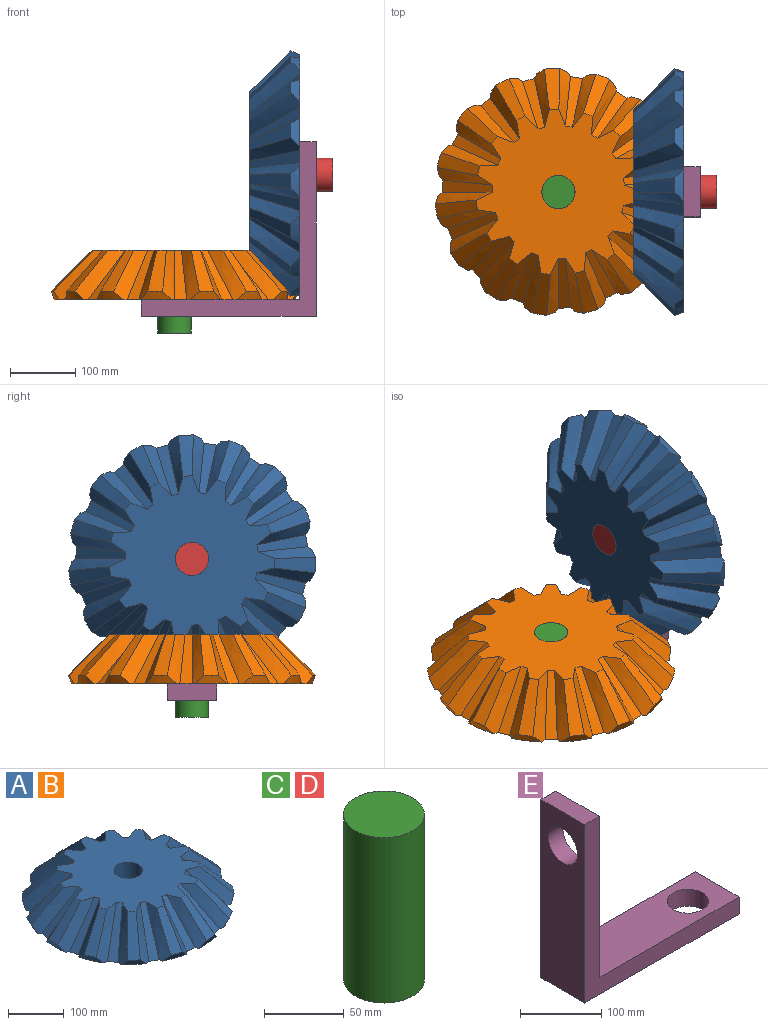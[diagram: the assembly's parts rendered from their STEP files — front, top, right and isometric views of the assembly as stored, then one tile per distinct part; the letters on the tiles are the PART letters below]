
ASSEMBLY  parts=5 mates=6
PART A: 78 faces, bbox 408.6x408.6x76.2 mm
  f0: plane 368.3x367.72mm, normal (0,0,-1), area 102263.9mm2, adj f2,f4,f6,f8,f10,f12,f14,f16
  f1: cone r=203.2mm half-angle=45deg, axis (0,0,-1), area 1668.1mm2, adj f2,f30,f33,f74
  f2: cone r=189.73mm half-angle=22.5deg, axis (0,0,1), area 520mm2, adj f0,f1,f33,f74
  f3: cone r=203.2mm half-angle=45deg, axis (0,0,-1), area 1668.1mm2, adj f4,f30,f71,f75
  f4: cone r=189.73mm half-angle=22.5deg, axis (0,0,1), area 520mm2, adj f0,f3,f71,f75
  f5: cone r=203.2mm half-angle=45deg, axis (0,0,-1), area 1668.1mm2, adj f6,f30,f68,f72
  f6: cone r=189.73mm half-angle=22.5deg, axis (0,0,1), area 520mm2, adj f0,f5,f68,f72
  f7: cone r=203.2mm half-angle=45deg, axis (0,0,-1), area 1668.1mm2, adj f8,f30,f65,f69
  f8: cone r=189.73mm half-angle=22.5deg, axis (0,0,1), area 520mm2, adj f0,f7,f65,f69
  f9: cone r=203.2mm half-angle=45deg, axis (0,0,-1), area 1668.1mm2, adj f10,f30,f62,f66
  f10: cone r=189.73mm half-angle=22.5deg, axis (0,0,1), area 520mm2, adj f0,f9,f62,f66
  f11: cone r=203.2mm half-angle=45deg, axis (0,0,-1), area 1668.1mm2, adj f12,f30,f59,f63
  f12: cone r=189.73mm half-angle=22.5deg, axis (0,0,1), area 520mm2, adj f0,f11,f59,f63
  f13: cone r=203.2mm half-angle=45deg, axis (0,0,-1), area 1668.1mm2, adj f14,f30,f56,f60
  f14: cone r=189.73mm half-angle=22.5deg, axis (0,0,1), area 520mm2, adj f0,f13,f56,f60
  f15: cone r=203.2mm half-angle=45deg, axis (0,0,-1), area 1668.1mm2, adj f16,f30,f53,f57
  f16: cone r=189.73mm half-angle=22.5deg, axis (0,0,1), area 520mm2, adj f0,f15,f53,f57
  f17: cone r=203.2mm half-angle=45deg, axis (0,0,-1), area 1668.1mm2, adj f18,f30,f50,f54
  f18: cone r=189.73mm half-angle=22.5deg, axis (0,0,1), area 520mm2, adj f0,f17,f50,f54
  f19: cone r=203.2mm half-angle=45deg, axis (0,0,-1), area 1668.1mm2, adj f20,f30,f47,f51
  f20: cone r=189.73mm half-angle=22.5deg, axis (0,0,1), area 520mm2, adj f0,f19,f47,f51
  f21: cone r=203.2mm half-angle=45deg, axis (0,0,-1), area 1668.1mm2, adj f22,f30,f44,f48
  f22: cone r=189.73mm half-angle=22.5deg, axis (0,0,1), area 520mm2, adj f0,f21,f44,f48
  f23: cone r=203.2mm half-angle=45deg, axis (0,0,-1), area 1668.1mm2, adj f24,f30,f41,f45
  f24: cone r=189.73mm half-angle=22.5deg, axis (0,0,1), area 520mm2, adj f0,f23,f41,f45
  f25: cone r=203.2mm half-angle=45deg, axis (0,0,-1), area 1668.1mm2, adj f26,f30,f38,f42
  f26: cone r=189.73mm half-angle=22.5deg, axis (0,0,1), area 520mm2, adj f0,f25,f38,f42
  f27: cone r=203.2mm half-angle=45deg, axis (0,0,-1), area 1668.1mm2, adj f28,f30,f35,f39
  f28: cone r=189.73mm half-angle=22.5deg, axis (0,0,1), area 520mm2, adj f0,f27,f35,f39
  f29: cone r=203.2mm half-angle=45deg, axis (0,0,-1), area 1668.1mm2, adj f30,f31,f32,f36
  f30: plane 253.72x252.54mm, normal (0,0,1), area 39255.5mm2, adj f1,f3,f5,f7,f9,f11,f13,f15
  f31: cone r=189.73mm half-angle=22.5deg, axis (0,0,1), area 520mm2, adj f0,f29,f32,f36
  f32: bspline ~101.6x76.2mm, area 2318.6mm2, adj f0,f29,f30,f31,f34
  f33: bspline ~99.08x76.2mm, area 2314.1mm2, adj f0,f1,f2,f30,f34
  f34: plane 76.2x76.2mm, normal (0.71,0,0.71), area 1594.3mm2, adj f0,f30,f32,f33
  f35: bspline ~81.96x76.2mm, area 2318.6mm2, adj f0,f27,f28,f30,f37
  f36: bspline ~103.67x76.2mm, area 2314.1mm2, adj f0,f29,f30,f31,f37
  f37: plane 76.2x75.63mm, normal (0.65,-0.29,0.71), area 1594.3mm2, adj f0,f30,f35,f36
  f38: bspline ~93.36x76.2mm, area 2318.6mm2, adj f0,f25,f26,f30,f40
  f39: bspline ~87.82x76.2mm, area 2314.1mm2, adj f0,f27,f28,f30,f40
  f40: plane 76.2x66.53mm, normal (0.47,-0.53,0.71), area 1594.3mm2, adj f0,f30,f38,f39
  f41: bspline ~104.88x76.2mm, area 2318.6mm2, adj f0,f23,f24,f30,f43
  f42: bspline ~86.68x76.2mm, area 2314.1mm2, adj f0,f25,f26,f30,f43
  f43: plane 77.04x76.2mm, normal (0.22,-0.67,0.71), area 1594.3mm2, adj f0,f30,f41,f42
  f44: bspline ~98.25x76.2mm, area 2318.6mm2, adj f0,f21,f22,f30,f46
  f45: bspline ~103.83x76.2mm, area 2314.1mm2, adj f0,f23,f24,f30,f46
  f46: plane 77.33x76.2mm, normal (-0.07,-0.7,0.71), area 1594.3mm2, adj f0,f30,f44,f45
  f47: bspline ~76.2x74.64mm, area 2318.6mm2, adj f0,f19,f20,f30,f49
  f48: bspline ~101.33x76.2mm, area 2314.1mm2, adj f0,f21,f22,f30,f49
  f49: plane 76.2x73.39mm, normal (-0.35,-0.61,0.71), area 1594.3mm2, adj f0,f30,f47,f48
  f50: bspline ~97.89x76.2mm, area 2318.6mm2, adj f0,f17,f18,f30,f52
  f51: bspline ~81.31x76.2mm, area 2314.1mm2, adj f0,f19,f20,f30,f52
  f52: plane 76.2x70.34mm, normal (-0.57,-0.42,0.71), area 1594.3mm2, adj f0,f30,f50,f51
  f53: bspline ~104.93x76.2mm, area 2318.6mm2, adj f0,f15,f16,f30,f55
  f54: bspline ~93.83x76.2mm, area 2314.1mm2, adj f0,f17,f18,f30,f55
  f55: plane 77.61x76.2mm, normal (-0.69,-0.15,0.71), area 1594.3mm2, adj f0,f30,f53,f54
  f56: bspline ~93.83x76.2mm, area 2318.6mm2, adj f0,f13,f14,f30,f58
  f57: bspline ~104.93x76.2mm, area 2314.1mm2, adj f0,f15,f16,f30,f58
  f58: plane 77.61x76.2mm, normal (-0.69,0.15,0.71), area 1594.3mm2, adj f0,f30,f56,f57
  f59: bspline ~81.31x76.2mm, area 2318.6mm2, adj f0,f11,f12,f30,f61
  f60: bspline ~97.89x76.2mm, area 2314.1mm2, adj f0,f13,f14,f30,f61
  f61: plane 76.2x70.34mm, normal (-0.57,0.42,0.71), area 1594.3mm2, adj f0,f30,f59,f60
  f62: bspline ~98.03x76.2mm, area 2318.6mm2, adj f0,f9,f10,f30,f64
  f63: bspline ~76.2x74.64mm, area 2314.1mm2, adj f0,f11,f12,f30,f64
  f64: plane 76.2x73.39mm, normal (-0.35,0.61,0.71), area 1594.3mm2, adj f0,f30,f62,f63
  f65: bspline ~101.1x76.2mm, area 2318.6mm2, adj f0,f7,f8,f30,f67
  f66: bspline ~98.25x76.2mm, area 2314.1mm2, adj f0,f9,f10,f30,f67
  f67: plane 77.33x76.2mm, normal (-0.07,0.7,0.71), area 1594.3mm2, adj f0,f30,f65,f66
  f68: bspline ~86.68x76.2mm, area 2318.6mm2, adj f0,f5,f6,f30,f70
  f69: bspline ~104.88x76.2mm, area 2314.1mm2, adj f0,f7,f8,f30,f70
  f70: plane 77.04x76.2mm, normal (0.22,0.67,0.71), area 1594.3mm2, adj f0,f30,f68,f69
  f71: bspline ~87.82x76.2mm, area 2318.6mm2, adj f0,f3,f4,f30,f73
  f72: bspline ~93.36x76.2mm, area 2314.1mm2, adj f0,f5,f6,f30,f73
  f73: plane 76.2x66.53mm, normal (0.47,0.53,0.71), area 1594.3mm2, adj f0,f30,f71,f72
  f74: bspline ~103.67x76.2mm, area 2318.6mm2, adj f0,f1,f2,f30,f76
  f75: bspline ~81.96x76.2mm, area 2314.1mm2, adj f0,f3,f4,f30,f76
  f76: plane 76.2x75.63mm, normal (0.65,0.29,0.71), area 1594.3mm2, adj f0,f30,f74,f75
  f77: cylinder r=25.4mm len=76.2mm, axis (0,0,1), area 12161mm2, adj f0,f30
PART B: same geometry as A
PART C: 3 faces, bbox 50.8x50.8x127 mm
  f0: cylinder r=25.4mm len=127mm, axis (0,0,-1), area 20268.3mm2, adj f1,f2
  f1: plane 50.8x50.8mm, normal (0,0,1), area 2026.8mm2, adj f0
  f2: plane 50.8x50.8mm, normal (0,0,-1), area 2026.8mm2, adj f0
PART D: same geometry as C
PART E: 10 faces, bbox 268x76.2x268 mm
  f0: plane 76.2x25.4mm, normal (0,0,1), area 1935.5mm2, adj f1,f5,f6,f7
  f1: plane 267.97x76.2mm, normal (-1,0,0), area 18392.5mm2, adj f0,f2,f6,f7,f9
  f2: plane 267.97x76.2mm, normal (0,0,-1), area 18392.5mm2, adj f1,f3,f6,f7,f8
  f3: plane 76.2x25.4mm, normal (1,0,0), area 1935.5mm2, adj f2,f4,f6,f7
  f4: plane 242.57x76.2mm, normal (0,0,1), area 16457mm2, adj f3,f5,f6,f7,f8
  f5: plane 242.57x76.2mm, normal (1,0,0), area 16457mm2, adj f0,f4,f6,f7,f9
  f6: plane 267.97x267.97mm, normal (0,-1,0), area 12967.7mm2, adj f0,f1,f2,f3,f4,f5
  f7: plane 267.97x267.97mm, normal (0,1,0), area 12967.7mm2, adj f0,f1,f2,f3,f4,f5
  f8: cylinder r=25.4mm len=50.8mm, axis (0,0,1), area 4053.7mm2, adj f2,f4
  f9: cylinder r=25.4mm len=50.8mm, axis (1,0,0), area 4053.7mm2, adj f1,f5
PLACE A rot(axis=(-0.46,-0.76,0.46),105.8deg) t=(191.77,0,217.17)mm
PLACE B rot(axis=(0,0,-1),63deg) t=(0,0,25.4)mm
PLACE C rot(axis=(0,0,1),27deg) t=(0,0,-25.4)mm
PLACE D rot(axis=(-0.7,-0.17,0.7),161deg) t=(242.57,0,217.17)mm
PLACE E rot(axis=(0,0,1),180deg) t=(217.17,0,0)mm
MATE cylindrical E.f8 <-> C.f0  axis (0,0,1) through (0,0,12.7)mm
MATE fastened C.f0 <-> B.f77  axis (0,0,1) through (0,0,101.6)mm
MATE revolute B.f77 <-> E.f8  axis (0,0,-1) through (0,0,25.4)mm
MATE revolute A.f1 <-> E.f9  axis (1,0,0) through (191.77,0,217.17)mm
MATE fastened D.f0 <-> A.f77  axis (-1,0,0) through (115.57,0,217.17)mm
MATE cylindrical E.f9 <-> D.f0  axis (-1,0,0) through (204.47,0,217.17)mm
